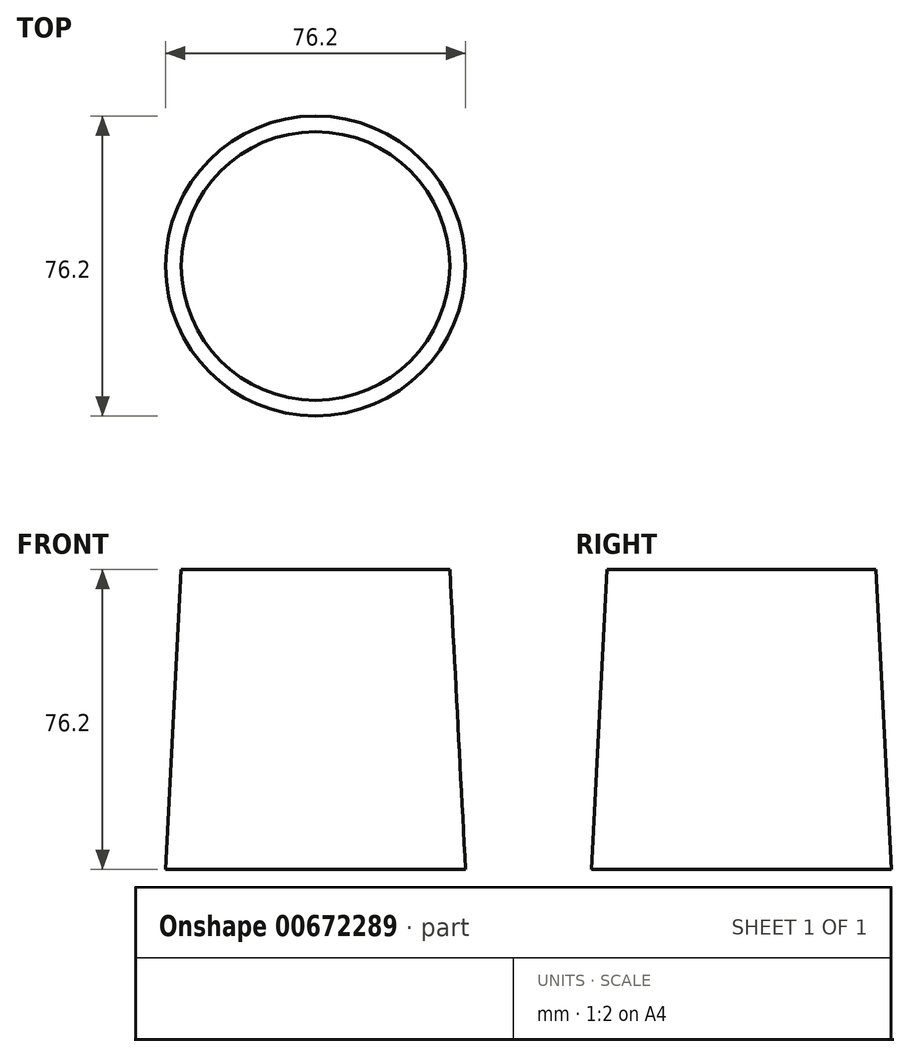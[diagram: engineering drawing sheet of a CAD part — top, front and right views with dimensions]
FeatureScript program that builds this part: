
annotation { "Feature Type Name" : "Feature", "Feature Type Description" : "" }
export const myFeature = defineFeature(function(context is Context, id is Id, definition is map)
    precondition{}
    {
        {
            var Q0;
            Q0=qCreatedBy(makeId("Top.planeOp"),FACE);
            var sketch = newSketch(context, id + "F0", { "sketchPlane" : qUnion([Q0])});
            skLineSegment(sketch, "E0", {"start": v(-69.23, 0) * mm, "end": v(68.9, 0) * mm, "construction": true});
            skCircle(sketch, "E1", {"center": v(0, 0) * mm, "radius": 38.1 * mm});
            skSolve(sketch);
        }
        {
            var Q0;
            Q0=makeQuery(id+"F0.imprint","IMPRINT",FACE,{"disambiguationData":[TD([[makeQuery(id+"F0.imprint","IMPRINT",EDGE,{"derivedFrom":sQuery(id+"F0.wireOp",EDGE,"E1")}),1.0]])]});
            extrude(context, id + "F1", {"entities" : qUnion([Q0]), "depth" : 76.2 * mm, "offsetDistance" : 25.4 * mm, "hasDraft" : true, "draftAngle" : 3 * degree, "draftPullDirection" : true});
        }
    });
